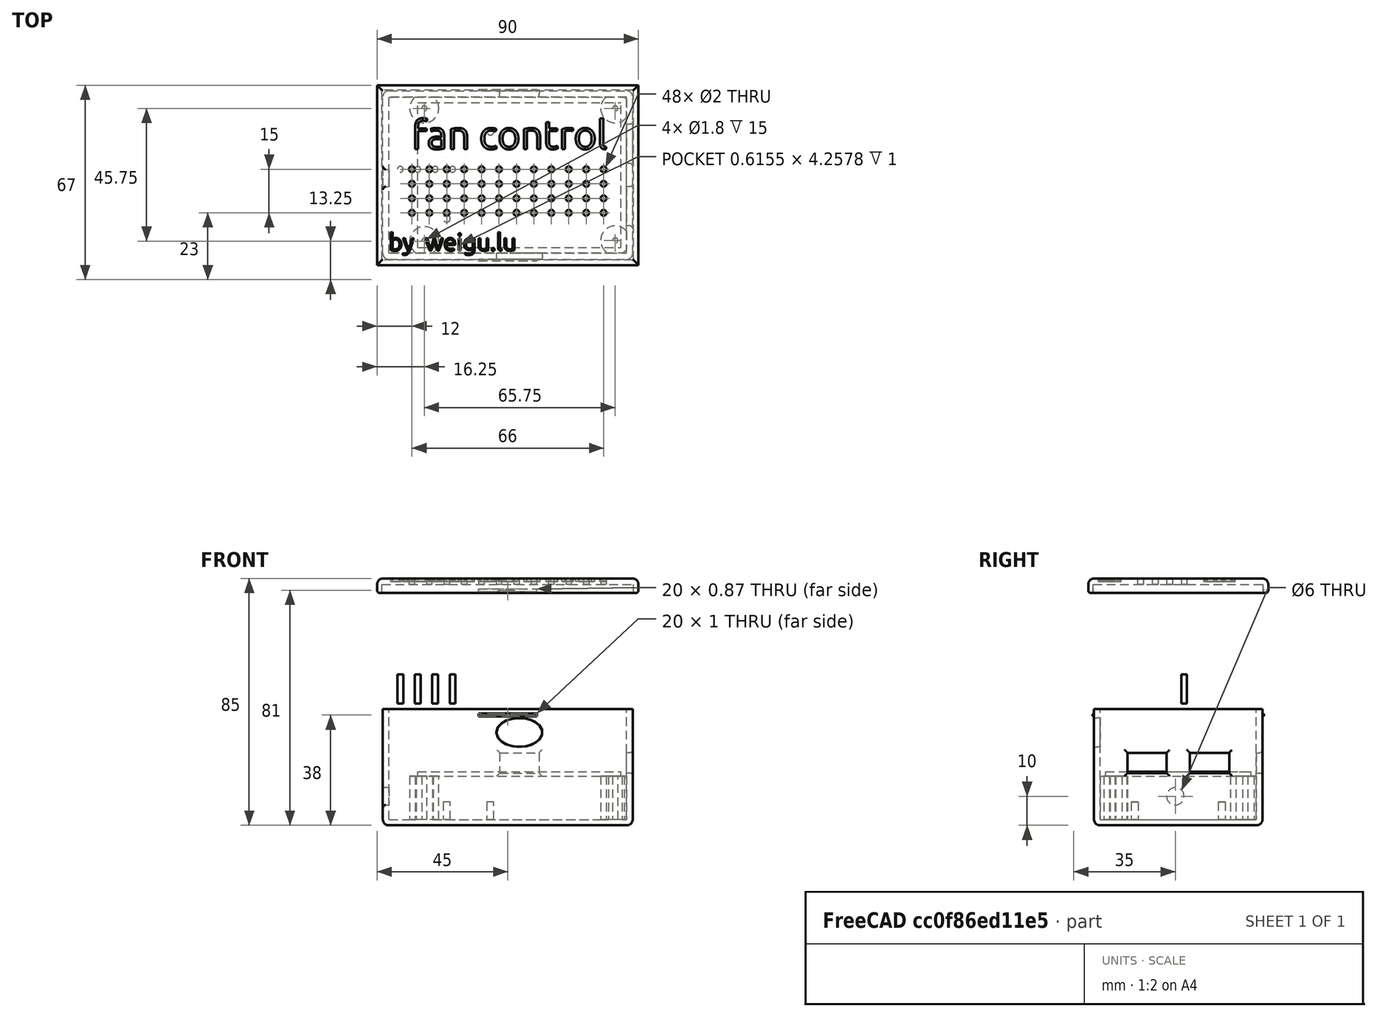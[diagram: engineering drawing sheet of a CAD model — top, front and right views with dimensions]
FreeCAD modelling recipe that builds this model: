
FCSTD DOCUMENT  (FreeCAD 0.20R29603 (Git))
Label: fan_control_case
License: Creative Commons Attribution-NonCommercial-ShareAlike
LicenseURL: http://creativecommons.org/licenses/by-nc-sa/4.0/
objects: Part::Cylinder×63, App::LinkGroup×17, Part::Cut×16, Part::Box×8, Part::Fillet×6, Part::MultiFuse×2, Part::Part2DObjectPython×2, Part::Extrusion×2, Part::Ellipsoid×1
note: 100 computed .brp shape members not serialized (recipe doc carries the construction recipe); baked Part::Feature solids carry a one-line shape summary decoded from their .brp

FEATURE [Part::Cylinder] Cylinder  label="PCB_Holder_1"
  Angle = 360
  AttacherType = Attacher::AttachEngine3D
  FirstAngle = 0
  Height = 22
  Placement = pos=(2.25,2.25,0) rot=(0,0,1;0rad)
  Radius = 0.9
  SecondAngle = 0
FEATURE [Part::Box] Box  label="PCB"
  AttacherType = Attacher::AttachEngine3D
  Height = 1.5
  Length = 70
  Placement = pos=(0,0,15) rot=(0,0,1;0rad)
  Width = 50
FEATURE [Part::Cylinder] Cylinder001  label="PCB_Holder_2"
  Angle = 360
  AttacherType = Attacher::AttachEngine3D
  FirstAngle = 0
  Height = 22
  Placement = pos=(2.25,48,0) rot=(0,0,1;0rad)
  Radius = 0.9
  SecondAngle = 0
FEATURE [Part::Cylinder] Cylinder002  label="PCB_Holder_3"
  Angle = 360
  AttacherType = Attacher::AttachEngine3D
  FirstAngle = 0
  Height = 22
  Placement = pos=(68,48,0) rot=(0,0,1;0rad)
  Radius = 0.9
  SecondAngle = 0
FEATURE [Part::Cylinder] Cylinder003  label="PCB1_Holder_002"
  Angle = 360
  AttacherType = Attacher::AttachEngine3D
  FirstAngle = 0
  Height = 22
  Placement = pos=(68,2.5,0) rot=(0,0,1;0rad)
  Radius = 0.9
  SecondAngle = 0
FEATURE [Part::Box] Box002  label="fan_socket_hole_1"
  AttacherType = Attacher::AttachEngine3D
  Height = 7
  Length = 13.5
  Placement = pos=(28.25,50,16) rot=(0,0,1;0rad)
  Width = 4
FEATURE [Part::Box] Box003  label="fan_socket_hole_2"
  AttacherType = Attacher::AttachEngine3D
  Height = 7
  Length = 13.5
  Placement = pos=(74,29,16) rot=(0,0,1;1.5708rad)
  Width = 4
FEATURE [Part::Box] Box004  label="fan_socket_hole_3"
  AttacherType = Attacher::AttachEngine3D
  Height = 7
  Length = 13.5
  Placement = pos=(74,7.5,16) rot=(0,0,1;1.5708rad)
  Width = 4
FEATURE [Part::Cylinder] Cylinder004  label="PCB2_Holder_1"
  Angle = 360
  AttacherType = Attacher::AttachEngine3D
  FirstAngle = 0
  Height = 6
  Placement = pos=(10,10,0) rot=(0,0,1;0rad)
  Radius = 1.2
  SecondAngle = 0
FEATURE [Part::Cylinder] Cylinder005  label="PCB2_Holder_2"
  Angle = 360
  AttacherType = Attacher::AttachEngine3D
  FirstAngle = 0
  Height = 6
  Placement = pos=(25,40,0) rot=(0,0,1;0rad)
  Radius = 1.2
  SecondAngle = 0
FEATURE [Part::Cylinder] Cylinder006  label="PCB_Holder_11"
  Angle = 360
  AttacherType = Attacher::AttachEngine3D
  FirstAngle = 0
  Height = 15
  Placement = pos=(2.25,2.25,0) rot=(0,0,1;0rad)
  Radius = 5
  SecondAngle = 0
FEATURE [Part::Cylinder] Cylinder007  label="PCB_Holder_12"
  Angle = 360
  AttacherType = Attacher::AttachEngine3D
  FirstAngle = 0
  Height = 15
  Placement = pos=(2.25,48,0) rot=(0,0,1;0rad)
  Radius = 5
  SecondAngle = 0
FEATURE [Part::Cylinder] Cylinder008  label="PCB_Holder_13"
  Angle = 360
  AttacherType = Attacher::AttachEngine3D
  FirstAngle = 0
  Height = 15
  Placement = pos=(68,48,0) rot=(0,0,1;0rad)
  Radius = 5
  SecondAngle = 0
FEATURE [Part::Cylinder] Cylinder009  label="PCB1_Holder_1"
  Angle = 360
  AttacherType = Attacher::AttachEngine3D
  FirstAngle = 0
  Height = 15
  Placement = pos=(68,2.5,0) rot=(0,0,1;0rad)
  Radius = 5
  SecondAngle = 0
FEATURE [Part::Box] Box005  label="Case_body_m"
  AttacherType = Attacher::AttachEngine3D
  Height = 40
  Length = 86
  Placement = pos=(-12,-4,-2) rot=(0,0,1;0rad)
  Width = 58
FEATURE [Part::Cut] Cut  label="PCB1_Holder_003"
  Base = -> Cylinder006
  Tool = -> Cylinder
FEATURE [Part::Cut] Cut001  label="PCB1_Holder_004"
  Base = -> Cylinder007
  Tool = -> Cylinder001
FEATURE [Part::Cut] Cut002  label="PCB1_Holder_005"
  Base = -> Cylinder008
  Tool = -> Cylinder002
FEATURE [Part::Cut] Cut003  label="PCB1_Holder_006"
  Base = -> Cylinder009
  Tool = -> Cylinder003
FEATURE [Part::Box] Box006  label="Case_body001"
  AttacherType = Attacher::AttachEngine3D
  Height = 40
  Length = 81.8
  Placement = pos=(-9.9,-1.9,0) rot=(0,0,1;0rad)
  Width = 53.8
FEATURE [Part::Cut] Cut004
  Base = -> Box005
  Tool = -> Box006
FEATURE [Part::Cylinder] Cylinder010  label="cable_hole"
  Angle = 360
  AttacherType = Attacher::AttachEngine3D
  FirstAngle = 0
  Height = 10
  Placement = pos=(-5,24,8) rot=(0,-1,0;1.5708rad)
  Radius = 3
  SecondAngle = 0
FEATURE [Part::Ellipsoid] Ellipsoid
  Angle1 = -90
  Angle2 = 90
  Angle3 = 360
  AttacherType = Attacher::AttachEngine3D
  Placement = pos=(35,-3,30) rot=(0,0,1;0rad)
  Radius1 = 6
  Radius2 = 10
  Radius3 = 10
FEATURE [Part::Cut] Cut005
  Base = -> Cut004
  Tool = -> Cylinder010
FEATURE [Part::Cut] Cut006
  Base = -> Cut005
  Tool = -> Ellipsoid
FEATURE [Part::Cut] Cut007
  Base = -> Cut006
  Tool = -> Box002
FEATURE [Part::Cut] Cut008
  Base = -> Cut007
  Tool = -> Box004
FEATURE [Part::Cut] Cut009
  Base = -> Cut008
  Tool = -> Box003
FEATURE [Part::MultiFuse] Fusion
  Shapes = -> [Cut009,Cut003,Cut002,Cut001,Cut,Cylinder005,Cylinder004]
FEATURE [Part::Box] Box007  label="Cube"
  AttacherType = Attacher::AttachEngine3D
  Height = 5
  Length = 90
  Placement = pos=(-14,-6,35) rot=(0,0,1;0rad)
  Width = 62
FEATURE [Part::Cylinder] Cylinder012  label="click1+"
  Angle = 360
  AttacherType = Attacher::AttachEngine3D
  FirstAngle = 0
  Height = 20
  Placement = pos=(41,54,36) rot=(0,-1,0;1.5708rad)
  Radius = 0.5
  SecondAngle = 0
FEATURE [Part::Cylinder] Cylinder013  label="click2+"
  Angle = 360
  AttacherType = Attacher::AttachEngine3D
  FirstAngle = 0
  Height = 20
  Placement = pos=(41,-4,36) rot=(0,-1,0;1.5708rad)
  Radius = 0.5
  SecondAngle = 0
FEATURE [Part::Cylinder] Cylinder014  label="click2-"
  Angle = 360
  AttacherType = Attacher::AttachEngine3D
  FirstAngle = 0
  Height = 20
  Placement = pos=(41,-4,36) rot=(0,-1,0;1.5708rad)
  Radius = 0.5
  SecondAngle = 0
FEATURE [Part::Cylinder] Cylinder015  label="click1-"
  Angle = 360
  AttacherType = Attacher::AttachEngine3D
  FirstAngle = 0
  Height = 20
  Placement = pos=(41,54,36) rot=(0,-1,0;1.5708rad)
  Radius = 0.5
  SecondAngle = 0
FEATURE [Part::MultiFuse] Fusion001  label="Case"
  Shapes = -> [Fusion,Cylinder012,Cylinder013]
FEATURE [Part::Box] Box008  label="Cube001"
  AttacherType = Attacher::AttachEngine3D
  Height = 5
  Length = 86.5
  Placement = pos=(-12.25,-4.25,33) rot=(0,0,1;0rad)
  Width = 58.5
FEATURE [Part::Cut] Cut010
  Base = -> Box007
  Tool = -> Box008
FEATURE [Part::Cut] Cut011
  Base = -> Cut010
  Tool = -> Cylinder015
FEATURE [Part::Cut] Cut012  label="Lid"
  Base = -> Cut011
  Tool = -> Cylinder014
FEATURE [Part::Fillet] Fillet
  Base = -> Fusion001
  Edges = 8 edges r=2: [Edge6,Edge7,Edge8,Edge15,Edge16,Edge17,Edge18,Edge28]
FEATURE [Part::Fillet] Fillet001
  Base = -> Fillet
  Edges = 8 edges r=1: [Edge56,Edge57,Edge58,Edge59,Edge60,Edge61,Edge62,Edge63]
FEATURE [Part::Fillet] Fillet002
  Base = -> Fillet001
  Edges = 4 edges r=1: [Edge74,Edge75,Edge76,Edge77]
FEATURE [Part::Fillet] Fillet003  label="case"
  Base = -> Fillet002
  Edges = 1 edges r=1: [Edge51]
FEATURE [Part::Fillet] Fillet004
  Base = -> Cut012
  Edges = 4 edges r=2: [Edge2,Edge7,Edge8,Edge9]
FEATURE [Part::Fillet] Fillet005  label="lid_nw"
  Base = -> Fillet004
  Edges = 4 edges r=1: [Edge2,Edge6,Edge11,Edge12]
FEATURE [Part::Part2DObjectPython] ShapeString  # Draft 2D object (typed FeaturePython)
  FontFile = /savit/freecad/fonts/truetype/ubuntu/Ubuntu-B.ttf
  MakeFace = true
  Size = 5
  String = fan control
  Tracking = 0
FEATURE [Part::Extrusion] Extrude
  Base = -> ShapeString
  Dir = (0,0,1)
  DirMode = 2
  FaceMakerClass = Part::FaceMakerBullseye
  LengthFwd = 2
  LengthRev = 0
  Placement = pos=(-2,34,39) rot=(0,0,1;0rad)
  Solid = false
  Symmetric = false
FEATURE [Part::Cut] Cut013
  Base = -> Fillet005
  Tool = -> Extrude
FEATURE [Part::Part2DObjectPython] ShapeString001  # Draft 2D object (typed FeaturePython)
  FontFile = /savit/freecad/fonts/truetype/ubuntu/Ubuntu-B.ttf
  MakeFace = true
  Size = 3
  String = by  weigu.lu
  Tracking = 0
FEATURE [Part::Extrusion] Extrude001
  Base = -> ShapeString001
  Dir = (0,0,1)
  DirMode = 2
  FaceMakerClass = Part::FaceMakerBullseye
  LengthFwd = 2
  LengthRev = 0
  Placement = pos=(-10,-1,39) rot=(0,0,1;0rad)
  Solid = false
  Symmetric = false
FEATURE [Part::Cut] Cut014  label="lid2"
  Base = -> Cut013
  Tool = -> Extrude001
FEATURE [Part::Cylinder] Cylinder016  label="Cylinder"
  Angle = 360
  AttacherType = Attacher::AttachEngine3D
  FirstAngle = 0
  Height = 10
  Placement = pos=(-6,27,40) rot=(0,0,1;0rad)
  Radius = 1
  SecondAngle = 0
FEATURE [Part::Cylinder] Cylinder017
  Angle = 360
  AttacherType = Attacher::AttachEngine3D
  FirstAngle = 0
  Height = 10
  Placement = pos=(6,27,40) rot=(0,0,1;0rad)
  Radius = 1
  SecondAngle = 0
FEATURE [Part::Cylinder] Cylinder018
  Angle = 360
  AttacherType = Attacher::AttachEngine3D
  FirstAngle = 0
  Height = 10
  Placement = pos=(0,27,40) rot=(0,0,1;0rad)
  Radius = 1
  SecondAngle = 0
FEATURE [Part::Cylinder] Cylinder019
  Angle = 360
  AttacherType = Attacher::AttachEngine3D
  FirstAngle = 0
  Height = 10
  Placement = pos=(12,27,40) rot=(0,0,1;0rad)
  Radius = 1
  SecondAngle = 0
FEATURE [Part::Cylinder] Cylinder020
  Angle = 360
  AttacherType = Attacher::AttachEngine3D
  FirstAngle = 0
  Height = 10
  Placement = pos=(-6,27,40) rot=(0,0,1;0rad)
  Radius = 1
  SecondAngle = 0
FEATURE [Part::Cylinder] Cylinder021
  Angle = 360
  AttacherType = Attacher::AttachEngine3D
  FirstAngle = 0
  Height = 10
  Placement = pos=(12,27,40) rot=(0,0,1;0rad)
  Radius = 1
  SecondAngle = 0
FEATURE [Part::Cylinder] Cylinder022
  Angle = 360
  AttacherType = Attacher::AttachEngine3D
  FirstAngle = 0
  Height = 10
  Placement = pos=(0,27,40) rot=(0,0,1;0rad)
  Radius = 1
  SecondAngle = 0
FEATURE [Part::Cylinder] Cylinder023
  Angle = 360
  AttacherType = Attacher::AttachEngine3D
  FirstAngle = 0
  Height = 10
  Placement = pos=(6,27,40) rot=(0,0,1;0rad)
  Radius = 1
  SecondAngle = 0
FEATURE [App::LinkGroup] LinkGroup
  ElementList = -> [Cylinder016,Cylinder019,Cylinder018,Cylinder017]
  LinkMode = 0
  Placement = pos=(28,0,0) rot=(0,0,1;0rad)
FEATURE [App::LinkGroup] LinkGroup001
  ElementList = -> [Cylinder020,Cylinder021,Cylinder022,Cylinder023]
  LinkMode = 0
  Placement = pos=(4,0,0) rot=(0,0,1;0rad)
FEATURE [Part::Cylinder] Cylinder024
  Angle = 360
  AttacherType = Attacher::AttachEngine3D
  FirstAngle = 0
  Height = 10
  Placement = pos=(-6,27,40) rot=(0,0,1;0rad)
  Radius = 1
  SecondAngle = 0
FEATURE [Part::Cylinder] Cylinder025
  Angle = 360
  AttacherType = Attacher::AttachEngine3D
  FirstAngle = 0
  Height = 10
  Placement = pos=(12,27,40) rot=(0,0,1;0rad)
  Radius = 1
  SecondAngle = 0
FEATURE [Part::Cylinder] Cylinder026
  Angle = 360
  AttacherType = Attacher::AttachEngine3D
  FirstAngle = 0
  Height = 10
  Placement = pos=(0,27,40) rot=(0,0,1;0rad)
  Radius = 1
  SecondAngle = 0
FEATURE [Part::Cylinder] Cylinder027
  Angle = 360
  AttacherType = Attacher::AttachEngine3D
  FirstAngle = 0
  Height = 10
  Placement = pos=(6,27,40) rot=(0,0,1;0rad)
  Radius = 1
  SecondAngle = 0
FEATURE [App::LinkGroup] LinkGroup002
  ElementList = -> [Cylinder024,Cylinder025,Cylinder026,Cylinder027]
  LinkMode = 0
  Placement = pos=(52,0,0) rot=(0,0,1;0rad)
FEATURE [App::LinkGroup] LinkGroup003
  ElementList = -> [LinkGroup,LinkGroup001,LinkGroup002]
  LinkMode = 0
FEATURE [Part::Cylinder] Cylinder028
  Angle = 360
  AttacherType = Attacher::AttachEngine3D
  FirstAngle = 0
  Height = 10
  Placement = pos=(-6,27,40) rot=(0,0,1;0rad)
  Radius = 1
  SecondAngle = 0
FEATURE [Part::Cylinder] Cylinder029
  Angle = 360
  AttacherType = Attacher::AttachEngine3D
  FirstAngle = 0
  Height = 10
  Placement = pos=(6,27,40) rot=(0,0,1;0rad)
  Radius = 1
  SecondAngle = 0
FEATURE [Part::Cylinder] Cylinder030
  Angle = 360
  AttacherType = Attacher::AttachEngine3D
  FirstAngle = 0
  Height = 10
  Placement = pos=(0,27,40) rot=(0,0,1;0rad)
  Radius = 1
  SecondAngle = 0
FEATURE [Part::Cylinder] Cylinder031
  Angle = 360
  AttacherType = Attacher::AttachEngine3D
  FirstAngle = 0
  Height = 10
  Placement = pos=(12,27,40) rot=(0,0,1;0rad)
  Radius = 1
  SecondAngle = 0
FEATURE [Part::Cylinder] Cylinder032
  Angle = 360
  AttacherType = Attacher::AttachEngine3D
  FirstAngle = 0
  Height = 10
  Placement = pos=(-6,27,40) rot=(0,0,1;0rad)
  Radius = 1
  SecondAngle = 0
FEATURE [Part::Cylinder] Cylinder033
  Angle = 360
  AttacherType = Attacher::AttachEngine3D
  FirstAngle = 0
  Height = 10
  Placement = pos=(12,27,40) rot=(0,0,1;0rad)
  Radius = 1
  SecondAngle = 0
FEATURE [Part::Cylinder] Cylinder034
  Angle = 360
  AttacherType = Attacher::AttachEngine3D
  FirstAngle = 0
  Height = 10
  Placement = pos=(0,27,40) rot=(0,0,1;0rad)
  Radius = 1
  SecondAngle = 0
FEATURE [Part::Cylinder] Cylinder035
  Angle = 360
  AttacherType = Attacher::AttachEngine3D
  FirstAngle = 0
  Height = 10
  Placement = pos=(6,27,40) rot=(0,0,1;0rad)
  Radius = 1
  SecondAngle = 0
FEATURE [Part::Cylinder] Cylinder036
  Angle = 360
  AttacherType = Attacher::AttachEngine3D
  FirstAngle = 0
  Height = 10
  Placement = pos=(-6,27,40) rot=(0,0,1;0rad)
  Radius = 1
  SecondAngle = 0
FEATURE [Part::Cylinder] Cylinder037
  Angle = 360
  AttacherType = Attacher::AttachEngine3D
  FirstAngle = 0
  Height = 10
  Placement = pos=(12,27,40) rot=(0,0,1;0rad)
  Radius = 1
  SecondAngle = 0
FEATURE [Part::Cylinder] Cylinder038
  Angle = 360
  AttacherType = Attacher::AttachEngine3D
  FirstAngle = 0
  Height = 10
  Placement = pos=(0,27,40) rot=(0,0,1;0rad)
  Radius = 1
  SecondAngle = 0
FEATURE [Part::Cylinder] Cylinder039
  Angle = 360
  AttacherType = Attacher::AttachEngine3D
  FirstAngle = 0
  Height = 10
  Placement = pos=(6,27,40) rot=(0,0,1;0rad)
  Radius = 1
  SecondAngle = 0
FEATURE [App::LinkGroup] LinkGroup004
  ElementList = -> [Cylinder028,Cylinder031,Cylinder030,Cylinder029]
  LinkMode = 0
  Placement = pos=(28,0,0) rot=(0,0,1;0rad)
FEATURE [App::LinkGroup] LinkGroup005
  ElementList = -> [Cylinder032,Cylinder033,Cylinder034,Cylinder035]
  LinkMode = 0
  Placement = pos=(4,0,0) rot=(0,0,1;0rad)
FEATURE [App::LinkGroup] LinkGroup006
  ElementList = -> [Cylinder036,Cylinder037,Cylinder038,Cylinder039]
  LinkMode = 0
  Placement = pos=(52,0,0) rot=(0,0,1;0rad)
FEATURE [App::LinkGroup] LinkGroup007
  ElementList = -> [LinkGroup004,LinkGroup005,LinkGroup006]
  LinkMode = 0
  Placement = pos=(0,-5,0) rot=(0,0,1;0rad)
FEATURE [Part::Cylinder] Cylinder040
  Angle = 360
  AttacherType = Attacher::AttachEngine3D
  FirstAngle = 0
  Height = 10
  Placement = pos=(-6,27,40) rot=(0,0,1;0rad)
  Radius = 1
  SecondAngle = 0
FEATURE [Part::Cylinder] Cylinder041
  Angle = 360
  AttacherType = Attacher::AttachEngine3D
  FirstAngle = 0
  Height = 10
  Placement = pos=(6,27,40) rot=(0,0,1;0rad)
  Radius = 1
  SecondAngle = 0
FEATURE [Part::Cylinder] Cylinder042
  Angle = 360
  AttacherType = Attacher::AttachEngine3D
  FirstAngle = 0
  Height = 10
  Placement = pos=(0,27,40) rot=(0,0,1;0rad)
  Radius = 1
  SecondAngle = 0
FEATURE [Part::Cylinder] Cylinder043
  Angle = 360
  AttacherType = Attacher::AttachEngine3D
  FirstAngle = 0
  Height = 10
  Placement = pos=(12,27,40) rot=(0,0,1;0rad)
  Radius = 1
  SecondAngle = 0
FEATURE [Part::Cylinder] Cylinder044
  Angle = 360
  AttacherType = Attacher::AttachEngine3D
  FirstAngle = 0
  Height = 10
  Placement = pos=(-6,27,40) rot=(0,0,1;0rad)
  Radius = 1
  SecondAngle = 0
FEATURE [Part::Cylinder] Cylinder045
  Angle = 360
  AttacherType = Attacher::AttachEngine3D
  FirstAngle = 0
  Height = 10
  Placement = pos=(12,27,40) rot=(0,0,1;0rad)
  Radius = 1
  SecondAngle = 0
FEATURE [Part::Cylinder] Cylinder046
  Angle = 360
  AttacherType = Attacher::AttachEngine3D
  FirstAngle = 0
  Height = 10
  Placement = pos=(0,27,40) rot=(0,0,1;0rad)
  Radius = 1
  SecondAngle = 0
FEATURE [Part::Cylinder] Cylinder047
  Angle = 360
  AttacherType = Attacher::AttachEngine3D
  FirstAngle = 0
  Height = 10
  Placement = pos=(6,27,40) rot=(0,0,1;0rad)
  Radius = 1
  SecondAngle = 0
FEATURE [Part::Cylinder] Cylinder048
  Angle = 360
  AttacherType = Attacher::AttachEngine3D
  FirstAngle = 0
  Height = 10
  Placement = pos=(-6,27,40) rot=(0,0,1;0rad)
  Radius = 1
  SecondAngle = 0
FEATURE [Part::Cylinder] Cylinder049
  Angle = 360
  AttacherType = Attacher::AttachEngine3D
  FirstAngle = 0
  Height = 10
  Placement = pos=(12,27,40) rot=(0,0,1;0rad)
  Radius = 1
  SecondAngle = 0
FEATURE [Part::Cylinder] Cylinder050
  Angle = 360
  AttacherType = Attacher::AttachEngine3D
  FirstAngle = 0
  Height = 10
  Placement = pos=(0,27,40) rot=(0,0,1;0rad)
  Radius = 1
  SecondAngle = 0
FEATURE [Part::Cylinder] Cylinder051
  Angle = 360
  AttacherType = Attacher::AttachEngine3D
  FirstAngle = 0
  Height = 10
  Placement = pos=(6,27,40) rot=(0,0,1;0rad)
  Radius = 1
  SecondAngle = 0
FEATURE [App::LinkGroup] LinkGroup008
  ElementList = -> [Cylinder040,Cylinder043,Cylinder042,Cylinder041]
  LinkMode = 0
  Placement = pos=(28,0,0) rot=(0,0,1;0rad)
FEATURE [App::LinkGroup] LinkGroup009
  ElementList = -> [Cylinder044,Cylinder045,Cylinder046,Cylinder047]
  LinkMode = 0
  Placement = pos=(4,0,0) rot=(0,0,1;0rad)
FEATURE [App::LinkGroup] LinkGroup010
  ElementList = -> [Cylinder048,Cylinder049,Cylinder050,Cylinder051]
  LinkMode = 0
  Placement = pos=(52,0,0) rot=(0,0,1;0rad)
FEATURE [App::LinkGroup] LinkGroup011
  ElementList = -> [LinkGroup008,LinkGroup009,LinkGroup010]
  LinkMode = 0
  Placement = pos=(0,-10,0) rot=(0,0,1;0rad)
FEATURE [Part::Cylinder] Cylinder052
  Angle = 360
  AttacherType = Attacher::AttachEngine3D
  FirstAngle = 0
  Height = 10
  Placement = pos=(-6,27,40) rot=(0,0,1;0rad)
  Radius = 1
  SecondAngle = 0
FEATURE [Part::Cylinder] Cylinder053
  Angle = 360
  AttacherType = Attacher::AttachEngine3D
  FirstAngle = 0
  Height = 10
  Placement = pos=(6,27,40) rot=(0,0,1;0rad)
  Radius = 1
  SecondAngle = 0
FEATURE [Part::Cylinder] Cylinder054
  Angle = 360
  AttacherType = Attacher::AttachEngine3D
  FirstAngle = 0
  Height = 10
  Placement = pos=(0,27,40) rot=(0,0,1;0rad)
  Radius = 1
  SecondAngle = 0
FEATURE [Part::Cylinder] Cylinder055
  Angle = 360
  AttacherType = Attacher::AttachEngine3D
  FirstAngle = 0
  Height = 10
  Placement = pos=(12,27,40) rot=(0,0,1;0rad)
  Radius = 1
  SecondAngle = 0
FEATURE [Part::Cylinder] Cylinder056
  Angle = 360
  AttacherType = Attacher::AttachEngine3D
  FirstAngle = 0
  Height = 10
  Placement = pos=(-6,27,40) rot=(0,0,1;0rad)
  Radius = 1
  SecondAngle = 0
FEATURE [Part::Cylinder] Cylinder057
  Angle = 360
  AttacherType = Attacher::AttachEngine3D
  FirstAngle = 0
  Height = 10
  Placement = pos=(12,27,40) rot=(0,0,1;0rad)
  Radius = 1
  SecondAngle = 0
FEATURE [Part::Cylinder] Cylinder058
  Angle = 360
  AttacherType = Attacher::AttachEngine3D
  FirstAngle = 0
  Height = 10
  Placement = pos=(0,27,40) rot=(0,0,1;0rad)
  Radius = 1
  SecondAngle = 0
FEATURE [Part::Cylinder] Cylinder059
  Angle = 360
  AttacherType = Attacher::AttachEngine3D
  FirstAngle = 0
  Height = 10
  Placement = pos=(6,27,40) rot=(0,0,1;0rad)
  Radius = 1
  SecondAngle = 0
FEATURE [Part::Cylinder] Cylinder060
  Angle = 360
  AttacherType = Attacher::AttachEngine3D
  FirstAngle = 0
  Height = 10
  Placement = pos=(-6,27,40) rot=(0,0,1;0rad)
  Radius = 1
  SecondAngle = 0
FEATURE [Part::Cylinder] Cylinder061
  Angle = 360
  AttacherType = Attacher::AttachEngine3D
  FirstAngle = 0
  Height = 10
  Placement = pos=(12,27,40) rot=(0,0,1;0rad)
  Radius = 1
  SecondAngle = 0
FEATURE [Part::Cylinder] Cylinder062
  Angle = 360
  AttacherType = Attacher::AttachEngine3D
  FirstAngle = 0
  Height = 10
  Placement = pos=(0,27,40) rot=(0,0,1;0rad)
  Radius = 1
  SecondAngle = 0
FEATURE [Part::Cylinder] Cylinder063
  Angle = 360
  AttacherType = Attacher::AttachEngine3D
  FirstAngle = 0
  Height = 10
  Placement = pos=(6,27,40) rot=(0,0,1;0rad)
  Radius = 1
  SecondAngle = 0
FEATURE [App::LinkGroup] LinkGroup012
  ElementList = -> [Cylinder052,Cylinder055,Cylinder054,Cylinder053]
  LinkMode = 0
  Placement = pos=(28,0,0) rot=(0,0,1;0rad)
FEATURE [App::LinkGroup] LinkGroup013
  ElementList = -> [Cylinder056,Cylinder057,Cylinder058,Cylinder059]
  LinkMode = 0
  Placement = pos=(4,0,0) rot=(0,0,1;0rad)
FEATURE [App::LinkGroup] LinkGroup014
  ElementList = -> [Cylinder060,Cylinder061,Cylinder062,Cylinder063]
  LinkMode = 0
  Placement = pos=(52,0,0) rot=(0,0,1;0rad)
FEATURE [App::LinkGroup] LinkGroup015
  ElementList = -> [LinkGroup012,LinkGroup013,LinkGroup014]
  LinkMode = 0
  Placement = pos=(0,-15,0) rot=(0,0,1;0rad)
FEATURE [App::LinkGroup] LinkGroup016
  ElementList = -> [LinkGroup003,LinkGroup007,LinkGroup011,LinkGroup015]
  LinkMode = 0
  Placement = pos=(0,0,-2) rot=(0,0,1;0rad)
FEATURE [Part::Cut] Cut015  label="lid"
  Base = -> Cut014
  Placement = pos=(0,0,43) rot=(0,0,1;0rad)
  Tool = -> LinkGroup016
